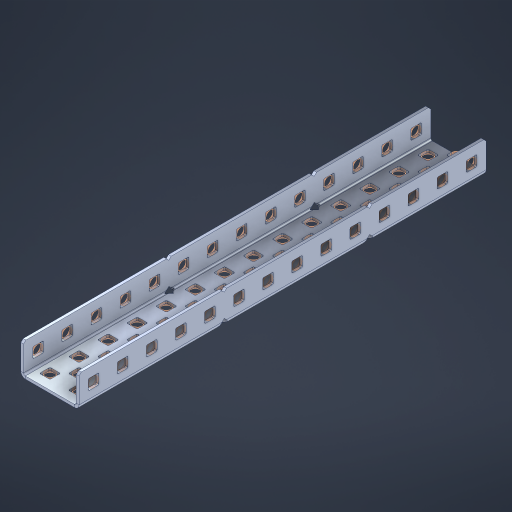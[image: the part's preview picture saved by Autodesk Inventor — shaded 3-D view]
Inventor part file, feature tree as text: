
AUTODESK INVENTOR PART (.ipt)
format: ipt  version: 2023 (Build 270158000, 158)  size: 1,115,648 bytes
history: native  units: in
note: dims shown in document units (in); Inventor stores cm internally (conversion verified against a paired STEP export)
features: other x77, extrude x68, sheet_metal_op x11, sketch x10, pattern_linear x2, mirror x1, chamfer x1
ambient origin geometry x8: Origin, YZ Plane, XZ Plane, XY Plane, X Axis, Y Axis, Z Axis, Center Point
bodies: Solid1 (feature_tree), Body (feature_tree)
feature tree (170):
  sheet_metal_op  "Flanges"
  other  "Flange Pattern Plane"
  other  "Flange Pattern Sketch"
  sheet_metal_op  "Flange Pattern"
  sheet_metal_op  "Body Pattern"
  pattern_linear  "Center Pattern"  Spacing1=0.0469in  [1 undecoded]
  other  "Arc Length"
  mirror  "Notch Mirror"
  pattern_linear  "Notch Pattern"  Spacing1=0.182in  [1 undecoded]
  chamfer  "End Chamfer"
  extrude  "Half Cut"  Depth=0.02in
  sketch  "Sketch1"  dims[d0=1.0in]
  other  "Plate1"
  sketch  "Sketch2"  dims[d1=7.0in]
  other  "Plate2"
  sheet_metal_op  "Bend1"
  sheet_metal_op  "Corner1"
  sketch  "Sketch3"  dims[d2=0.0469in]
  sketch  "Sketch7"  dims[d3=0.0469in]
  other  "Srf1"
  other  "Srf2"
  sketch  "Sketch8"  dims[d4=0.0234in]
  sketch  "Sketch9"  dims[d5=0.0938in]
  other  "Srf91"
  sheet_metal_op  "Body Pattern Sketch"
  other  "Srf92"
  sketch  "Sketch13"  dims[d6=0.0469in]
  sketch  "Sketch14"  dims[d7=0.5in d8=90.0deg d9=0.0312in]
  sketch  "Sketch15"  dims[d10=0.1875in]
  sketch  "Sketch16"  dims[d11=0.0469in d12=0.0469in d16=0.182in d17=0.02in d18=0.0469in d19=0.0in d20=0.25in d21=0.25in d38=5.5118in d40=0.5in d41=0.7874in d43=1.0in d46=0.172in d47=1.0in d48=0.0in d49=0.182in d50=0.02in d51=0.25in d52=0.25in d53=0.0469in d54=0.0in d55=0.172in d56=1.0in d57=0.0in d58=0.25in d60=5.5118in d62=0.5in d63=0.7874in d65=0.5in d85=0.1227in d86=0.1659in d88=0.04in d89=0.0469in d90=0.0in d91=0.04in d92=0.0491in d95=2.5in d96=0.04in d97=0.25in d98=45.0deg d99=0.25in d100=0.5in d101=0.0in d102=2.497in d106=0.182in d107=0.02in d108=0.5in d109=0.5in d110=0.0469in d111=0.0in d112=0.172in d113=0.5in d114=0.0in d117=0.5in d118=0.5in d119=0.5in]
  other  "Srf786"
  other  "Srf823"
  other  "Srf824"
  other  "Srf825"
  other  "Srf826"
  other  "Srf827"
  other  "Srf828"
  other  "Srf829"
  other  "Srf856"
  other  "Srf857"
  other  "Srf858"
  other  "Srf859"
  other  "Srf860"
  other  "Srf861"
  other  "Srf862"
  other  "Srf889"
  other  "Srf890"
  other  "Srf891"
  other  "Srf892"
  other  "Srf893"
  other  "Srf894"
  other  "Srf895"
  other  "Srf896"
  other  "Srf922"
  other  "Srf923"
  other  "Srf924"
  other  "Srf925"
  other  "Srf926"
  other  "Srf959"
  other  "Srf960"
  other  "Srf961"
  other  "Srf962"
  other  "Srf963"
  other  "Srf996"
  other  "Srf997"
  other  "Srf998"
  other  "Srf999"
  other  "Srf1000"
  other  "Srf1143"
  other  "Srf1144"
  other  "Srf1145"
  other  "Srf1146"
  other  "Srf1147"
  other  "Srf1148"
  other  "Srf1149"
  other  "Srf1150"
  other  "Srf1151"
  other  "Srf1152"
  other  "Srf1153"
  other  "Srf1154"
  other  "Srf1155"
  other  "Srf1156"
  other  "Srf1199"
  other  "Srf1200"
  other  "Srf1201"
  other  "Srf1202"
  other  "Srf1203"
  other  "Srf1204"
  other  "Srf1205"
  other  "Srf1206"
  other  "Srf1207"
  other  "Srf1208"
  other  "Srf1209"
  other  "Srf1210"
  other  "Srf1211"
  other  "Srf1212"
  sheet_metal_op  "Flange Stamp"
  sheet_metal_op  "Flange Circle"
  sheet_metal_op  "Body Stamp"
  sheet_metal_op  "Body Circle"
  other  "Center Stamp"
  other  "Center Circle"
  sheet_metal_op  "Notch"
  extrude  "ExtrusionSrf2"  Depth=0.0469in
  extrude  "ExtrusionSrf92"  TaperAngle=0.0deg  [1 undecoded]
  extrude  "ExtrusionSrf823"  Depth=0.5in
  extrude  "ExtrusionSrf824"  Depth=0.5in
  extrude  "ExtrusionSrf825"  Depth=0.5in
  extrude  "ExtrusionSrf826"  Depth=0.5in
  extrude  "ExtrusionSrf827"  Depth=1.0in TaperAngle=0.0deg
  extrude  "ExtrusionSrf828"  Depth=0.5in
  extrude  "ExtrusionSrf829"  Depth=0.02in
  extrude  "ExtrusionSrf856"  Depth=0.5in
  extrude  "ExtrusionSrf857"  Depth=0.5in
  extrude  "ExtrusionSrf858"  Depth=0.0469in
  extrude  "ExtrusionSrf859"  TaperAngle=0.0deg  [1 undecoded]
  extrude  "ExtrusionSrf860"  Depth=0.5in
  extrude  "ExtrusionSrf861"  Depth=1.0in TaperAngle=0.0deg
  extrude  "ExtrusionSrf862"  Depth=0.5in
  extrude  "ExtrusionSrf889"  Depth=0.5in
  extrude  "ExtrusionSrf890"  Depth=0.5in
  extrude  "ExtrusionSrf891"  Depth=0.5in
  extrude  "ExtrusionSrf892"  Depth=0.5in
  extrude  "ExtrusionSrf893"  Depth=0.5in
  extrude  "ExtrusionSrf894"  Depth=0.0469in
  extrude  "ExtrusionSrf895"  TaperAngle=0.0deg  [1 undecoded]
  extrude  "ExtrusionSrf896"  Depth=0.5in
  extrude  "ExtrusionSrf922"  Depth=0.5in
  extrude  "ExtrusionSrf923"  Depth=2.5in
  extrude  "ExtrusionSrf924"  Depth=0.5in TaperAngle=45.0deg
  extrude  "ExtrusionSrf925"  Depth=0.5in
  extrude  "ExtrusionSrf926"  Depth=0.5in TaperAngle=0.0deg
  extrude  "ExtrusionSrf959"  Depth=0.5in
  extrude  "ExtrusionSrf960"  Depth=0.5in
  extrude  "ExtrusionSrf961"  Depth=0.02in
  extrude  "ExtrusionSrf962"  Depth=0.5in
  extrude  "ExtrusionSrf963"  Depth=0.5in
  extrude  "ExtrusionSrf996"  Depth=0.0469in
  extrude  "ExtrusionSrf997"  TaperAngle=0.0deg  [1 undecoded]
  extrude  "ExtrusionSrf998"  Depth=0.5in
  extrude  "ExtrusionSrf999"  Depth=0.5in TaperAngle=0.0deg
  extrude  "ExtrusionSrf1000"  Depth=0.5in
  extrude  "ExtrusionSrf1143"  Depth=0.5in
  extrude  "ExtrusionSrf1144"  Depth=0.5in
  extrude  "ExtrusionSrf1145"  [1 undecoded]
  extrude  "ExtrusionSrf1146"  [1 undecoded]
  extrude  "ExtrusionSrf1147"  [1 undecoded]
  extrude  "ExtrusionSrf1148"  [1 undecoded]
  extrude  "ExtrusionSrf1149"  [1 undecoded]
  extrude  "ExtrusionSrf1150"  [1 undecoded]
  extrude  "ExtrusionSrf1151"  [1 undecoded]
  extrude  "ExtrusionSrf1152"  [1 undecoded]
  extrude  "ExtrusionSrf1153"  [1 undecoded]
  extrude  "ExtrusionSrf1154"  [1 undecoded]
  extrude  "ExtrusionSrf1155"  [1 undecoded]
  extrude  "ExtrusionSrf1156"  [1 undecoded]
  extrude  "ExtrusionSrf1199"  [1 undecoded]
  extrude  "ExtrusionSrf1200"  [1 undecoded]
  extrude  "ExtrusionSrf1201"  [1 undecoded]
  extrude  "ExtrusionSrf1202"  [1 undecoded]
  extrude  "ExtrusionSrf1203"  [1 undecoded]
  extrude  "ExtrusionSrf1204"  [1 undecoded]
  extrude  "ExtrusionSrf1205"  [1 undecoded]
  extrude  "ExtrusionSrf1206"  [1 undecoded]
  extrude  "ExtrusionSrf1207"  [1 undecoded]
  extrude  "ExtrusionSrf1208"  [1 undecoded]
  extrude  "ExtrusionSrf1209"  [1 undecoded]
  extrude  "ExtrusionSrf1210"  [1 undecoded]
  extrude  "ExtrusionSrf1211"  [1 undecoded]
  extrude  "ExtrusionSrf1212"  [1 undecoded]
note: 32 required parameter values undecoded (feature->parameter linkage not recoverable at this tier; creation-order binding heuristic only, values carry confidence <= 0.55)
